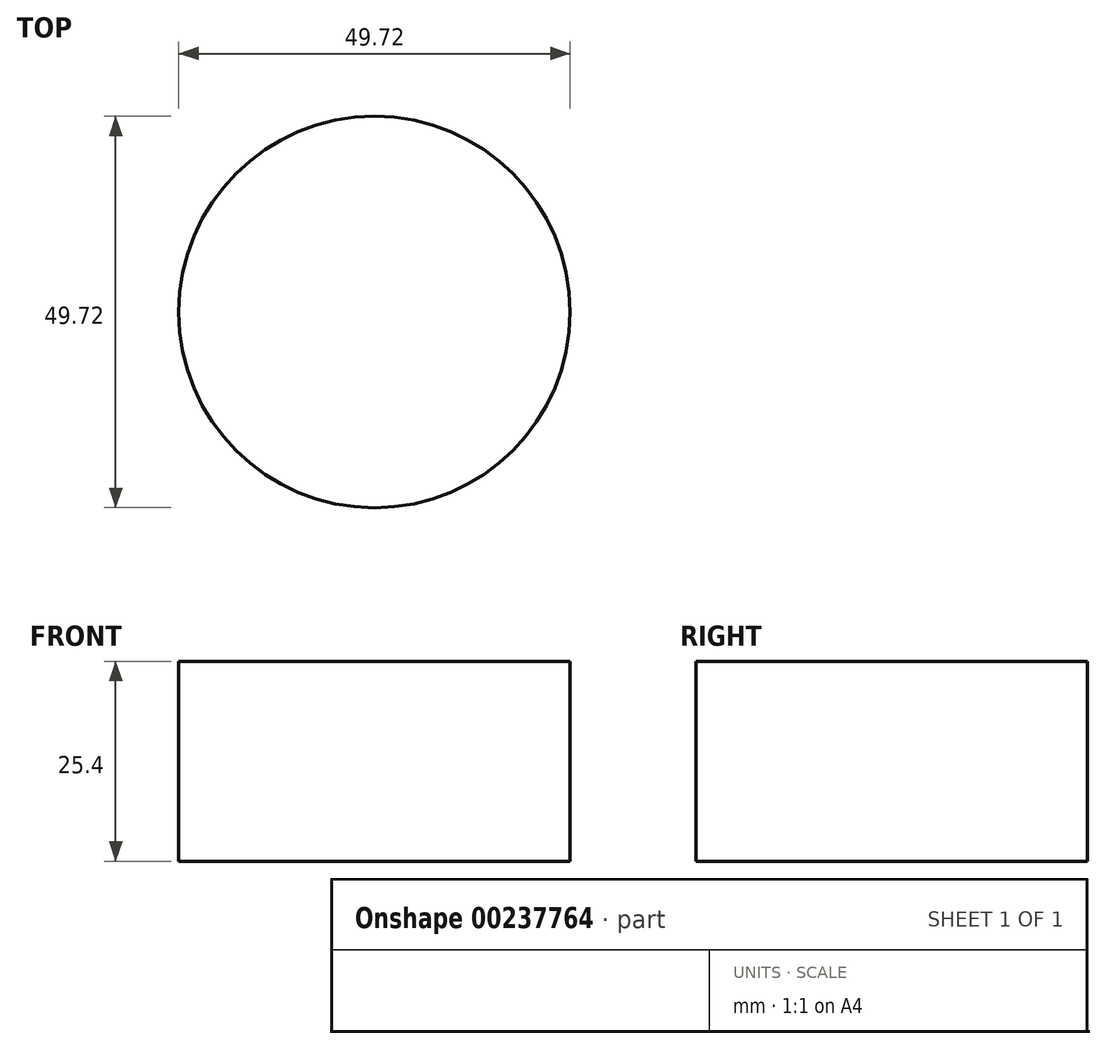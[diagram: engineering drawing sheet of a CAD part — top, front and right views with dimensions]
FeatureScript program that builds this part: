
annotation { "Feature Type Name" : "Feature", "Feature Type Description" : "" }
export const myFeature = defineFeature(function(context is Context, id is Id, definition is map)
    precondition{}
    {
        {
            var Q0;
            Q0=qCreatedBy(makeId("Top.planeOp"),FACE);
            var sketch = newSketch(context, id + "F0", { "sketchPlane" : qUnion([Q0])});
            skCircle(sketch, "E0", {"center": v(0, 0) * mm, "radius": 24.86 * mm});
            skSolve(sketch);
        }
        {
            var Q0;
            Q0 = qSketchRegion(id + "F0", true);
            extrude(context, id + "F1", {"entities" : qUnion([Q0]), "depth" : 25.4 * mm});
        }
    });
